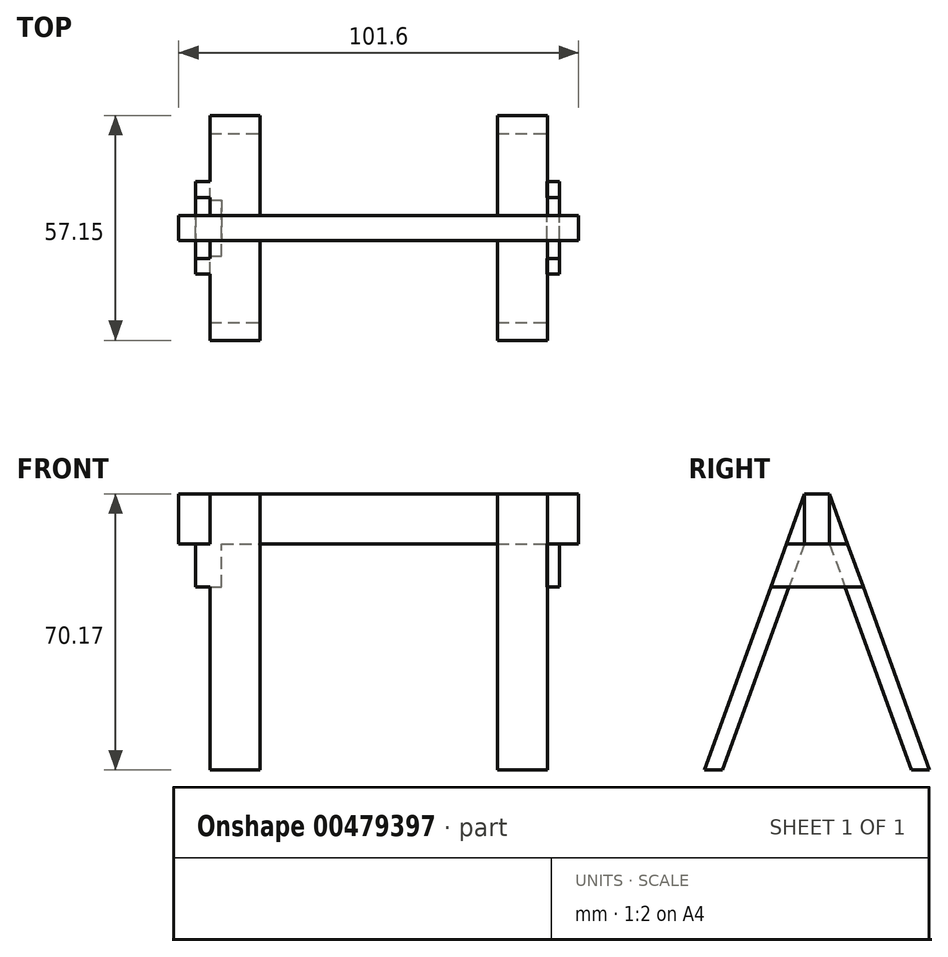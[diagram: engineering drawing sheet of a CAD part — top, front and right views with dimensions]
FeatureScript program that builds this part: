
annotation { "Feature Type Name" : "Feature", "Feature Type Description" : "" }
export const myFeature = defineFeature(function(context is Context, id is Id, definition is map)
    precondition{}
    {
        {
            var Q0;
            Q0=qCreatedBy(makeId("Right.planeOp"),FACE);
            var sketch = newSketch(context, id + "F0", { "sketchPlane" : qUnion([Q0])});
            skLineSegment(sketch, "E0", {"start": v(-6.35, 30.58) * mm, "end": v(-6.35, 17.88) * mm});
            skLineSegment(sketch, "E1", {"start": v(-6.35, 17.88) * mm, "end": v(0, 17.88) * mm});
            skLineSegment(sketch, "E2", {"start": v(0, 17.88) * mm, "end": v(0, 30.58) * mm});
            skLineSegment(sketch, "E3", {"start": v(0, 30.58) * mm, "end": v(-6.35, 30.58) * mm});
            skLineSegment(sketch, "E4", {"start": v(-6.35, 30.58) * mm, "end": v(-31.75, -39.59) * mm});
            skLineSegment(sketch, "E5", {"start": v(0, 30.58) * mm, "end": v(25.4, -39.59) * mm});
            skLineSegment(sketch, "E6", {"start": v(-6.35, 17.88) * mm, "end": v(-27.15, -39.59) * mm});
            skLineSegment(sketch, "E7", {"start": v(0, 17.88) * mm, "end": v(20.8, -39.59) * mm});
            skLineSegment(sketch, "E8", {"start": v(-27.15, -39.59) * mm, "end": v(-31.75, -39.59) * mm});
            skLineSegment(sketch, "E9", {"start": v(20.8, -39.59) * mm, "end": v(25.4, -39.59) * mm});
            skLineSegment(sketch, "E10", {"start": v(-6.35, 17.88) * mm, "end": v(-10.95, 17.88) * mm});
            skLineSegment(sketch, "E11", {"start": v(0, 17.88) * mm, "end": v(4.6, 17.88) * mm});
            skLineSegment(sketch, "E12", {"start": v(-14.9, 6.95) * mm, "end": v(8.55, 6.95) * mm});
            skSolve(sketch);
        }
        {
            var Q0;
            Q0=makeQuery(id+"F0.imprint","IMPRINT",FACE,{"disambiguationData":[TD([[makeQuery(id+"F0.imprint","IMPRINT",EDGE,{"derivedFrom":sQuery(id+"F0.wireOp",EDGE,"E0")}),1.0]])]});
            extrude(context, id + "F1", {"entities" : qUnion([Q0]), "oppositeDirection" : true, "depth" : 101.6 * mm});
        }
        {
            var Q0;
            {var subQ0=sQuery(id+"F0.wireOp",EDGE,"E10");Q0=makeQuery(id+"F0.imprint","IMPRINT",FACE,{"disambiguationData":[TD([[makeQuery(id+"F0.imprint","IMPRINT",EDGE,{"derivedFrom":subQ0}),1.0]])]});}
            var Q1;
            {var subQ0=sQuery(id+"F0.wireOp",EDGE,"E0");Q1=makeQuery(id+"F0.imprint","IMPRINT",FACE,{"disambiguationData":[TD([[makeQuery(id+"F0.imprint","IMPRINT",EDGE,{"derivedFrom":subQ0}),-1.0]])]});}
            var Q2;
            {var subQ0=sQuery(id+"F0.wireOp",EDGE,"E2");Q2=makeQuery(id+"F0.imprint","IMPRINT",FACE,{"disambiguationData":[TD([[makeQuery(id+"F0.imprint","IMPRINT",EDGE,{"derivedFrom":subQ0}),-1.0]])]});}
            var Q3;
            {var subQ0=sQuery(id+"F0.wireOp",EDGE,"E11");Q3=makeQuery(id+"F0.imprint","IMPRINT",FACE,{"disambiguationData":[TD([[makeQuery(id+"F0.imprint","IMPRINT",EDGE,{"derivedFrom":subQ0}),-1.0]])]});}
            var Q4;
            {var subQ0=sQuery(id+"F0.wireOp",EDGE,"E9");Q4=makeQuery(id+"F0.imprint","IMPRINT",FACE,{"disambiguationData":[TD([[makeQuery(id+"F0.imprint","IMPRINT",EDGE,{"derivedFrom":subQ0}),1.0]])]});}
            var Q5;
            {var subQ0=sQuery(id+"F0.wireOp",EDGE,"E8");Q5=makeQuery(id+"F0.imprint","IMPRINT",FACE,{"disambiguationData":[TD([[makeQuery(id+"F0.imprint","IMPRINT",EDGE,{"derivedFrom":subQ0}),-1.0]])]});}
            extrude(context, id + "F2", {"entities" : qUnion([Q0, Q1, Q2, Q3, Q4, Q5]), "oppositeDirection" : true, "depth" : 20.65 * mm, "hasSecondDirection" : true, "secondDirectionOppositeDirection" : true, "secondDirectionDepth" : 7.95 * mm});
        }
        {
            var Q0;
            {var subQ0=sQuery(id+"F0.wireOp",EDGE,"E0");Q0=makeQuery(id+"F0.imprint","IMPRINT",FACE,{"disambiguationData":[TD([[makeQuery(id+"F0.imprint","IMPRINT",EDGE,{"derivedFrom":subQ0}),-1.0]])]});}
            var Q1;
            {var subQ0=sQuery(id+"F0.wireOp",EDGE,"E2");Q1=makeQuery(id+"F0.imprint","IMPRINT",FACE,{"disambiguationData":[TD([[makeQuery(id+"F0.imprint","IMPRINT",EDGE,{"derivedFrom":subQ0}),-1.0]])]});}
            var Q2;
            {var subQ0=sQuery(id+"F0.wireOp",EDGE,"E11");Q2=makeQuery(id+"F0.imprint","IMPRINT",FACE,{"disambiguationData":[TD([[makeQuery(id+"F0.imprint","IMPRINT",EDGE,{"derivedFrom":subQ0}),-1.0]])]});}
            var Q3;
            {var subQ0=sQuery(id+"F0.wireOp",EDGE,"E9");Q3=makeQuery(id+"F0.imprint","IMPRINT",FACE,{"disambiguationData":[TD([[makeQuery(id+"F0.imprint","IMPRINT",EDGE,{"derivedFrom":subQ0}),1.0]])]});}
            var Q4;
            {var subQ0=sQuery(id+"F0.wireOp",EDGE,"E10");Q4=makeQuery(id+"F0.imprint","IMPRINT",FACE,{"disambiguationData":[TD([[makeQuery(id+"F0.imprint","IMPRINT",EDGE,{"derivedFrom":subQ0}),1.0]])]});}
            var Q5;
            {var subQ0=sQuery(id+"F0.wireOp",EDGE,"E8");Q5=makeQuery(id+"F0.imprint","IMPRINT",FACE,{"disambiguationData":[TD([[makeQuery(id+"F0.imprint","IMPRINT",EDGE,{"derivedFrom":subQ0}),-1.0]])]});}
            extrude(context, id + "F3", {"entities" : qUnion([Q0, Q1, Q2, Q3, Q4, Q5]), "operationType" : NewBodyOperationType.ADD, "oppositeDirection" : true, "depth" : 93.68 * mm, "hasSecondDirection" : true, "secondDirectionOppositeDirection" : true, "secondDirectionDepth" : 80.98 * mm});
        }
        {
            var Q0;
            {var subQ0=sQuery(id+"F0.wireOp",EDGE,"E1");Q0=makeQuery(id+"F0.imprint","IMPRINT",FACE,{"disambiguationData":[TD([[makeQuery(id+"F0.imprint","IMPRINT",EDGE,{"derivedFrom":subQ0}),-1.0]])]});}
            var Q1;
            {var subQ0=sQuery(id+"F0.wireOp",EDGE,"E10");Q1=makeQuery(id+"F0.imprint","IMPRINT",FACE,{"disambiguationData":[TD([[makeQuery(id+"F0.imprint","IMPRINT",EDGE,{"derivedFrom":subQ0}),1.0]])]});}
            var Q2;
            {var subQ0=sQuery(id+"F0.wireOp",EDGE,"E11");Q2=makeQuery(id+"F0.imprint","IMPRINT",FACE,{"disambiguationData":[TD([[makeQuery(id+"F0.imprint","IMPRINT",EDGE,{"derivedFrom":subQ0}),-1.0]])]});}
            extrude(context, id + "F4", {"entities" : qUnion([Q0, Q1, Q2]), "oppositeDirection" : true, "depth" : 8.08 * mm, "hasSecondDirection" : true, "secondDirectionOppositeDirection" : true, "secondDirectionDepth" : 4.83 * mm});
        }
        {
            var Q0;
            {var subQ0=sQuery(id+"F0.wireOp",EDGE,"E10");Q0=makeQuery(id+"F0.imprint","IMPRINT",FACE,{"disambiguationData":[TD([[makeQuery(id+"F0.imprint","IMPRINT",EDGE,{"derivedFrom":subQ0}),1.0]])]});}
            var Q1;
            {var subQ0=sQuery(id+"F0.wireOp",EDGE,"E1");Q1=makeQuery(id+"F0.imprint","IMPRINT",FACE,{"disambiguationData":[TD([[makeQuery(id+"F0.imprint","IMPRINT",EDGE,{"derivedFrom":subQ0}),-1.0]])]});}
            var Q2;
            {var subQ0=sQuery(id+"F0.wireOp",EDGE,"E11");Q2=makeQuery(id+"F0.imprint","IMPRINT",FACE,{"disambiguationData":[TD([[makeQuery(id+"F0.imprint","IMPRINT",EDGE,{"derivedFrom":subQ0}),-1.0]])]});}
            extrude(context, id + "F5", {"entities" : qUnion([Q0, Q1, Q2]), "operationType" : NewBodyOperationType.ADD, "oppositeDirection" : true, "depth" : 97.28 * mm, "hasSecondDirection" : true, "secondDirectionOppositeDirection" : true, "secondDirectionDepth" : 90.68 * mm});
        }
    });
